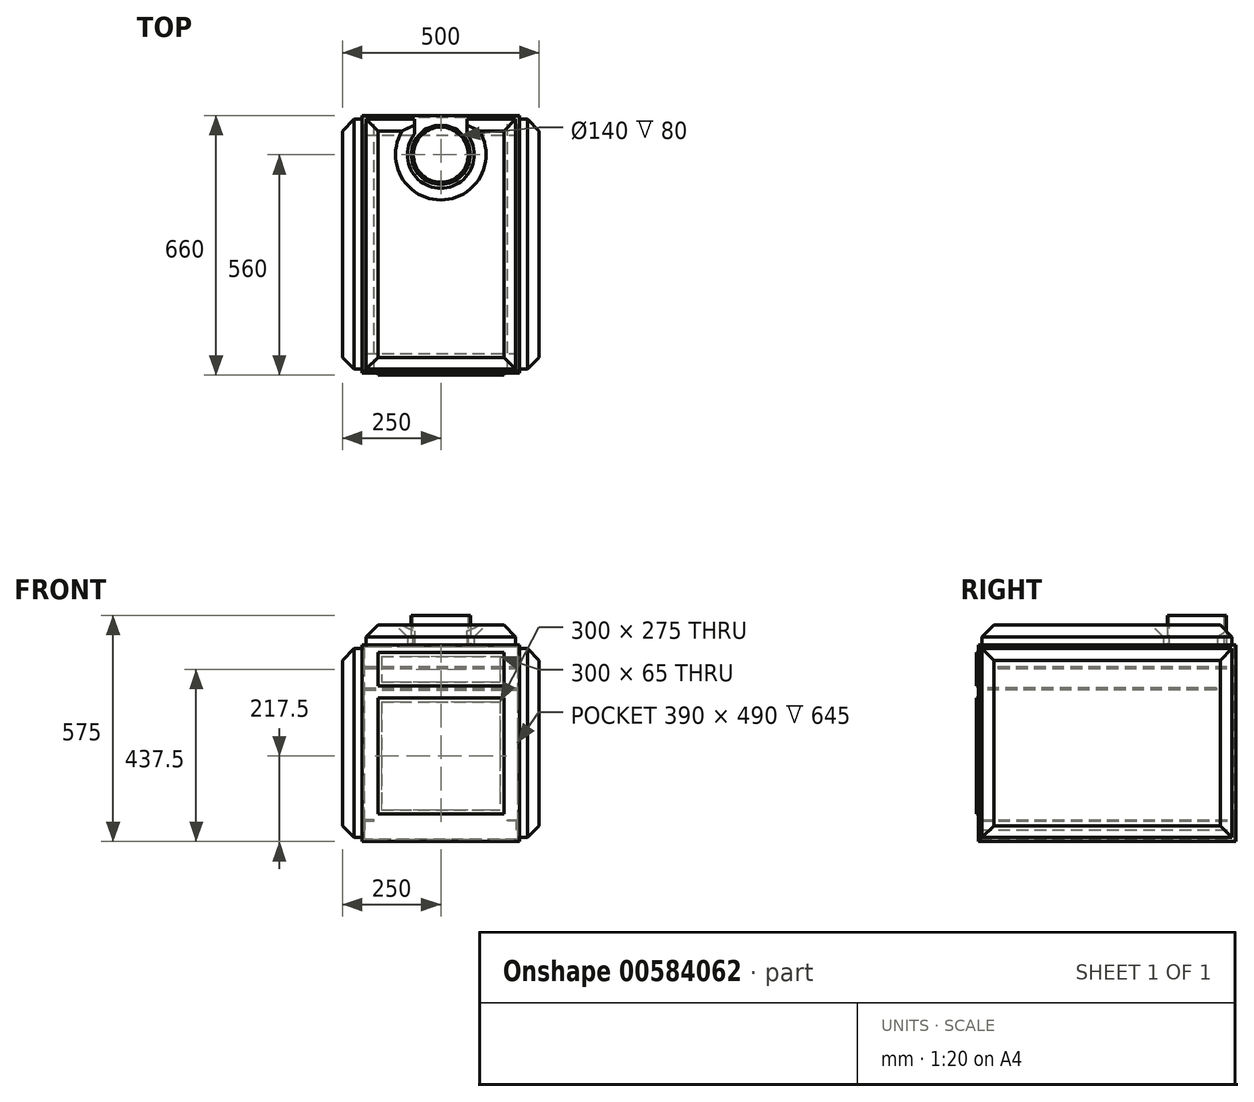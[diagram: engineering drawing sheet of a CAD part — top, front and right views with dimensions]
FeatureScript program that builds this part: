
annotation { "Feature Type Name" : "Feature", "Feature Type Description" : "" }
export const myFeature = defineFeature(function(context is Context, id is Id, definition is map)
    precondition{}
    {
        {
            assignVariable(context, id + "F0", {"name" : "Thickness", "anyValue" : 5});
        }
        {
            var Q0;
            Q0=qCreatedBy(makeId("Top.planeOp"),FACE);
            var sketch = newSketch(context, id + "F1", { "sketchPlane" : qUnion([Q0])});
            skLineSegment(sketch, "E0.bottom", {"start": v(200, 0) * mm, "end": v(-200, 0) * mm});
            skLineSegment(sketch, "E0.top", {"start": v(200, 650) * mm, "end": v(-200, 650) * mm});
            skLineSegment(sketch, "E0.left", {"start": v(200, 0) * mm, "end": v(200, 650) * mm});
            skLineSegment(sketch, "E0.right", {"start": v(-200, 0) * mm, "end": v(-200, 650) * mm});
            skPoint(sketch, "E0.middle", {"position": v(0, 325) * mm});
            skSolve(sketch);
        }
        {
            var Q0;
            Q0=qSketchRegion(id+"F1",true);
            extrude(context, id + "F2", {"entities" : qUnion([Q0]), "depth" : 500 * mm, "offsetDistance" : 25 * mm});
        }
        {
            var Q0;
            Q0=makeQuery(id+"F2.opExtrude","SWEPT_FACE",FACE,{"disambiguationData":[OSD([sQuery(id+"F1.wireOp",EDGE,"E0.bottom")])]});
            var Q1;
            Q1=makeQuery(id+"F2.opExtrude","SWEPT_BODY",BODY,{"disambiguationData":[OSD([sQuery(id+"F1.wireOp",EDGE,"E0.bottom"),sQuery(id+"F1.wireOp",EDGE,"E0.top"),sQuery(id+"F1.wireOp",EDGE,"E0.left"),sQuery(id+"F1.wireOp",EDGE,"E0.right")])]});
            shell(context, id + "F3", {"entities" : qUnion([Q0]), "parts" : qUnion([Q1]), "thickness" : (getVariable(context, 'Thickness')) * mm});
        }
        {
            var Q0;
            Q0=makeQuery(id+"F3.opShell","OFFSET_FACE",FACE,{"disambiguationData":[OSD([sQuery(id+"F1.wireOp",EDGE,"E0.top")])]});
            var sketch = newSketch(context, id + "F4", { "sketchPlane" : qUnion([Q0])});
            skLineSegment(sketch, "E1.bottom", {"start": v(-195, 445) * mm, "end": v(195, 445) * mm});
            skLineSegment(sketch, "E1.top", {"start": v(-195, 440) * mm, "end": v(195, 440) * mm});
            skLineSegment(sketch, "E1.left", {"start": v(-195, 445) * mm, "end": v(-195, 440) * mm});
            skLineSegment(sketch, "E1.right", {"start": v(195, 445) * mm, "end": v(195, 440) * mm});
            skSolve(sketch);
        }
        {
            var Q0;
            Q0=qSketchRegion(id+"F4",true);
            extrude(context, id + "F5", {"entities" : qUnion([Q0]), "depth" : 600 * mm, "offsetDistance" : 25 * mm});
        }
        {
            var Q0;
            Q0=makeQuery(id+"F2.opExtrude","SWEPT_FACE",FACE,{"disambiguationData":[OSD([sQuery(id+"F1.wireOp",EDGE,"E0.bottom")])]});
            var sketch = newSketch(context, id + "F6", { "sketchPlane" : qUnion([Q0])});
            skLineSegment(sketch, "E2.bottom", {"start": v(-195, 390) * mm, "end": v(195, 390) * mm});
            skLineSegment(sketch, "E2.top", {"start": v(-195, 385) * mm, "end": v(195, 385) * mm});
            skLineSegment(sketch, "E2.left", {"start": v(-195, 390) * mm, "end": v(-195, 385) * mm});
            skLineSegment(sketch, "E2.right", {"start": v(195, 390) * mm, "end": v(195, 385) * mm});
            skSolve(sketch);
        }
        {
            var Q0;
            Q0=qSketchRegion(id+"F6",true);
            extrude(context, id + "F7", {"entities" : qUnion([Q0]), "oppositeDirection" : true, "depth" : 600 * mm, "offsetDistance" : 25 * mm});
        }
        {
            var Q0;
            Q0=makeQuery(id+"F3.opShell","OFFSET_FACE",FACE,{"disambiguationData":[OSD([sQuery(id+"F1.wireOp",EDGE,"E0.top")])]});
            var sketch = newSketch(context, id + "F8", { "sketchPlane" : qUnion([Q0])});
            skLineSegment(sketch, "E3", {"start": v(-170, 55) * mm, "end": v(-195, 55) * mm});
            skLineSegment(sketch, "E4", {"start": v(-195, 55) * mm, "end": v(-195, 30) * mm});
            skLineSegment(sketch, "E5", {"start": v(-195, 30) * mm, "end": v(-192, 30) * mm});
            skLineSegment(sketch, "E6", {"start": v(-192, 30) * mm, "end": v(-192, 52) * mm});
            skLineSegment(sketch, "E7", {"start": v(-192, 52) * mm, "end": v(-170, 52) * mm});
            skLineSegment(sketch, "E8", {"start": v(-170, 52) * mm, "end": v(-170, 55) * mm});
            skLineSegment(sketch, "E9.MirrorCS", {"start": v(195, 30) * mm, "end": v(192, 30) * mm});
            skLineSegment(sketch, "E10.MirrorCS", {"start": v(170, 52) * mm, "end": v(170, 55) * mm});
            skLineSegment(sketch, "E11.MirrorCS", {"start": v(195, 55) * mm, "end": v(195, 30) * mm});
            skLineSegment(sketch, "E12.MirrorCS", {"start": v(170, 55) * mm, "end": v(195, 55) * mm});
            skLineSegment(sketch, "E13.MirrorCS", {"start": v(192, 30) * mm, "end": v(192, 52) * mm});
            skLineSegment(sketch, "E14.MirrorCS", {"start": v(192, 52) * mm, "end": v(170, 52) * mm});
            skSolve(sketch);
        }
        {
            var Q0;
            Q0=qSketchRegion(id+"F8",true);
            var Q1;
            Q1=makeQuery(id+"F2.opExtrude","SWEPT_FACE",FACE,{"disambiguationData":[OSD([sQuery(id+"F1.wireOp",EDGE,"E0.bottom")])]});
            extrude(context, id + "F9", {"entities" : qUnion([Q0]), "endBound" : BoundingType.UP_TO_SURFACE, "depth" : 25 * mm, "endBoundEntityFace" : qUnion([Q1]), "offsetDistance" : 25 * mm});
        }
        {
            var Q0;
            Q0=makeQuery(id+"F2.opExtrude","CAP_FACE",FACE,{"disambiguationData":[OSD([sQuery(id+"F1.wireOp",EDGE,"E0.bottom"),sQuery(id+"F1.wireOp",EDGE,"E0.top"),sQuery(id+"F1.wireOp",EDGE,"E0.left"),sQuery(id+"F1.wireOp",EDGE,"E0.right")])],"isStart":false});
            var sketch = newSketch(context, id + "F10", { "sketchPlane" : qUnion([Q0])});
            skCircle(sketch, "E15", {"center": v(0, 550) * mm, "radius": 75 * mm});
            skSolve(sketch);
        }
        {
            var Q0;
            Q0=qSketchRegion(id+"F10",true);
            extrude(context, id + "F11", {"entities" : qUnion([Q0]), "operationType" : NewBodyOperationType.ADD, "depth" : 75 * mm, "offsetDistance" : 25 * mm});
        }
        {
            var Q0;
            Q0=makeQuery(id+"F11.opExtrude","CAP_FACE",FACE,{"disambiguationData":[OSD([sQuery(id+"F10.wireOp",EDGE,"E15")])],"isStart":false});
            var sketch = newSketch(context, id + "F12", { "sketchPlane" : qUnion([Q0])});
            skCircle(sketch, "E16", {"center": v(0, 550) * mm, "radius": 70 * mm});
            skSolve(sketch);
        }
        {
            var Q0;
            Q0=qSketchRegion(id+"F12",true);
            extrude(context, id + "F13", {"entities" : qUnion([Q0]), "operationType" : NewBodyOperationType.REMOVE, "endBound" : BoundingType.UP_TO_NEXT, "oppositeDirection" : true, "depth" : 25 * mm, "offsetDistance" : 25 * mm});
        }
        {
            var Q0;
            Q0=makeQuery(id+"F2.opExtrude","SWEPT_FACE",FACE,{"disambiguationData":[OSD([sQuery(id+"F1.wireOp",EDGE,"E0.bottom")])]});
            var sketch = newSketch(context, id + "F14", { "sketchPlane" : qUnion([Q0])});
            skLineSegment(sketch, "E17.bottom", {"start": v(-200, 500) * mm, "end": v(200, 500) * mm});
            skLineSegment(sketch, "E17.top", {"start": v(-200, 0) * mm, "end": v(200, 0) * mm});
            skLineSegment(sketch, "E17.left", {"start": v(-200, 500) * mm, "end": v(-200, 0) * mm});
            skLineSegment(sketch, "E17.right", {"start": v(200, 500) * mm, "end": v(200, 0) * mm});
            skLineSegment(sketch, "E18.bottom", {"start": v(-150, 355) * mm, "end": v(150, 355) * mm});
            skLineSegment(sketch, "E18.top", {"start": v(-150, 80) * mm, "end": v(150, 80) * mm});
            skLineSegment(sketch, "E18.left", {"start": v(-150, 355) * mm, "end": v(-150, 80) * mm});
            skLineSegment(sketch, "E18.right", {"start": v(150, 355) * mm, "end": v(150, 80) * mm});
            skLineSegment(sketch, "E19.bottom", {"start": v(-150, 470) * mm, "end": v(150, 470) * mm});
            skLineSegment(sketch, "E19.top", {"start": v(-150, 405) * mm, "end": v(150, 405) * mm});
            skLineSegment(sketch, "E19.left", {"start": v(-150, 470) * mm, "end": v(-150, 405) * mm});
            skLineSegment(sketch, "E19.right", {"start": v(150, 470) * mm, "end": v(150, 405) * mm});
            skSolve(sketch);
        }
        {
            var Q0;
            Q0=qSketchRegion(id+"F14",true);
            extrude(context, id + "F15", {"entities" : qUnion([Q0]), "depth" : (getVariable(context, 'Thickness')) * mm, "offsetDistance" : 25 * mm});
        }
        {
            var Q0;
            Q0=makeQuery(id+"F15.opExtrude","CAP_FACE",FACE,{"disambiguationData":[OSD([sQuery(id+"F14.wireOp",EDGE,"E17.bottom"),sQuery(id+"F14.wireOp",EDGE,"E17.top"),sQuery(id+"F14.wireOp",EDGE,"E17.left"),sQuery(id+"F14.wireOp",EDGE,"E17.right"),sQuery(id+"F14.wireOp",EDGE,"E18.bottom"),sQuery(id+"F14.wireOp",EDGE,"E18.top"),sQuery(id+"F14.wireOp",EDGE,"E18.left"),sQuery(id+"F14.wireOp",EDGE,"E18.right"),sQuery(id+"F14.wireOp",EDGE,"E19.bottom"),sQuery(id+"F14.wireOp",EDGE,"E19.top"),sQuery(id+"F14.wireOp",EDGE,"E19.left"),sQuery(id+"F14.wireOp",EDGE,"E19.right")])],"isStart":false});
            var sketch = newSketch(context, id + "F16", { "sketchPlane" : qUnion([Q0])});
            skLineSegment(sketch, "E20.bottom", {"start": v(-160, 480) * mm, "end": v(160, 480) * mm});
            skLineSegment(sketch, "E20.top", {"start": v(-160, 395) * mm, "end": v(160, 395) * mm});
            skLineSegment(sketch, "E20.left", {"start": v(-160, 480) * mm, "end": v(-160, 395) * mm});
            skLineSegment(sketch, "E20.right", {"start": v(160, 480) * mm, "end": v(160, 395) * mm});
            skLineSegment(sketch, "E21.bottom", {"start": v(-160, 365) * mm, "end": v(160, 365) * mm});
            skLineSegment(sketch, "E21.top", {"start": v(-160, 70) * mm, "end": v(160, 70) * mm});
            skLineSegment(sketch, "E21.left", {"start": v(-160, 365) * mm, "end": v(-160, 70) * mm});
            skLineSegment(sketch, "E21.right", {"start": v(160, 365) * mm, "end": v(160, 70) * mm});
            skSolve(sketch);
        }
        {
            var Q0;
            Q0=qSketchRegion(id+"F16",true);
            extrude(context, id + "F17", {"entities" : qUnion([Q0]), "depth" : (getVariable(context, 'Thickness')) * mm, "offsetDistance" : 25 * mm});
        }
        {
            var Q0;
            Q0=makeQuery(id+"F2.opExtrude","SWEPT_FACE",FACE,{"disambiguationData":[OSD([sQuery(id+"F1.wireOp",EDGE,"E0.right")])]});
            var sketch = newSketch(context, id + "F18", { "sketchPlane" : qUnion([Q0])});
            skLineSegment(sketch, "E22.bottom", {"start": v(-640, 490) * mm, "end": v(-5, 490) * mm});
            skLineSegment(sketch, "E22.top", {"start": v(-640, 10) * mm, "end": v(-5, 10) * mm});
            skLineSegment(sketch, "E22.left", {"start": v(-640, 490) * mm, "end": v(-640, 10) * mm});
            skLineSegment(sketch, "E22.right", {"start": v(-5, 490) * mm, "end": v(-5, 10) * mm});
            skSolve(sketch);
        }
        {
            var Q0;
            Q0 = qSketchRegion(id + "F18", true);
            extrude(context, id + "F19", {"entities" : qUnion([Q0]), "depth" : 50 * mm, "offsetDistance" : 25 * mm});
        }
        {
            var Q0;
            Q0=makeQuery(id+"F19.opExtrude","SWEPT_BODY",BODY,{"disambiguationData":[OSD([sQuery(id+"F18.wireOp",EDGE,"E22.bottom"),sQuery(id+"F18.wireOp",EDGE,"E22.top"),sQuery(id+"F18.wireOp",EDGE,"E22.left"),sQuery(id+"F18.wireOp",EDGE,"E22.right")])]});
            var Q1;
            Q1=qCreatedBy(makeId("Right.planeOp"),FACE);
            mirror(context, id + "F20", {"entities" : qUnion([Q0]), "mirrorPlane" : qUnion([Q1])});
        }
        {
            var Q0;
            Q0=makeQuery(id+"F2.opExtrude","CAP_FACE",FACE,{"disambiguationData":[OSD([sQuery(id+"F1.wireOp",EDGE,"E0.bottom"),sQuery(id+"F1.wireOp",EDGE,"E0.top"),sQuery(id+"F1.wireOp",EDGE,"E0.left"),sQuery(id+"F1.wireOp",EDGE,"E0.right")])],"isStart":false});
            var sketch = newSketch(context, id + "F21", { "sketchPlane" : qUnion([Q0])});
            skLineSegment(sketch, "E23.bottom", {"start": v(-190, 640) * mm, "end": v(-67.09, 640) * mm});
            skLineSegment(sketch, "E23.top", {"start": v(-190, 5) * mm, "end": v(190, 5) * mm});
            skLineSegment(sketch, "E23.left", {"start": v(-190, 640) * mm, "end": v(-190, 5) * mm});
            skLineSegment(sketch, "E23.right", {"start": v(190, 640) * mm, "end": v(190, 5) * mm});
            skArc(sketch, "E24", {"start": v(-67.09, 602.2) * mm, "mid": v(0, 465) * mm, "end": v(67.09, 602.2) * mm});
            skLineSegment(sketch, "E25", {"start": v(-67.09, 602.2) * mm, "end": v(-67.09, 640) * mm});
            skLineSegment(sketch, "E26", {"start": v(67.09, 602.2) * mm, "end": v(67.09, 640) * mm});
            skLineSegment(sketch, "E27", {"start": v(0, 550) * mm, "end": v(0, 705.28) * mm, "construction": true});
            skLineSegment(sketch, "E28.trimOffspring", {"start": v(67.09, 640) * mm, "end": v(190, 640) * mm});
            skSolve(sketch);
        }
        {
            var Q0;
            Q0 = qSketchRegion(id + "F21", true);
            extrude(context, id + "F22", {"entities" : qUnion([Q0]), "depth" : 50 * mm, "offsetDistance" : 25 * mm});
        }
        {
            var Q0;
            Q0=makeQuery(id+"F19.opExtrude","CAP_FACE",FACE,{"disambiguationData":[OSD([sQuery(id+"F18.wireOp",EDGE,"E22.bottom"),sQuery(id+"F18.wireOp",EDGE,"E22.top"),sQuery(id+"F18.wireOp",EDGE,"E22.left"),sQuery(id+"F18.wireOp",EDGE,"E22.right")])],"isStart":false});
            var Q1;
            Q1=makeQuery(id+"F22.opExtrude","CAP_FACE",FACE,{"disambiguationData":[OSD([sQuery(id+"F21.wireOp",EDGE,"E23.bottom"),sQuery(id+"F21.wireOp",EDGE,"E23.top"),sQuery(id+"F21.wireOp",EDGE,"E23.left"),sQuery(id+"F21.wireOp",EDGE,"E23.right"),sQuery(id+"F21.wireOp",EDGE,"E24"),sQuery(id+"F21.wireOp",EDGE,"E25"),sQuery(id+"F21.wireOp",EDGE,"E26"),sQuery(id+"F21.wireOp",EDGE,"E28.trimOffspring")])],"isStart":false});
            var Q2;
            Q2=makeQuery(id+"F20.opPattern","COPY",FACE,{"derivedFrom":makeQuery(id+"F19.opExtrude","CAP_FACE",FACE,{"disambiguationData":[OSD([sQuery(id+"F18.wireOp",EDGE,"E22.bottom"),sQuery(id+"F18.wireOp",EDGE,"E22.top"),sQuery(id+"F18.wireOp",EDGE,"E22.left"),sQuery(id+"F18.wireOp",EDGE,"E22.right")])],"isStart":false}),"instanceName":"1"});
            chamfer(context, id + "F23", {"entities" : qUnion([Q0, Q1, Q2]), "width" : 30 * mm, "tangentPropagation" : true});
        }
    });
